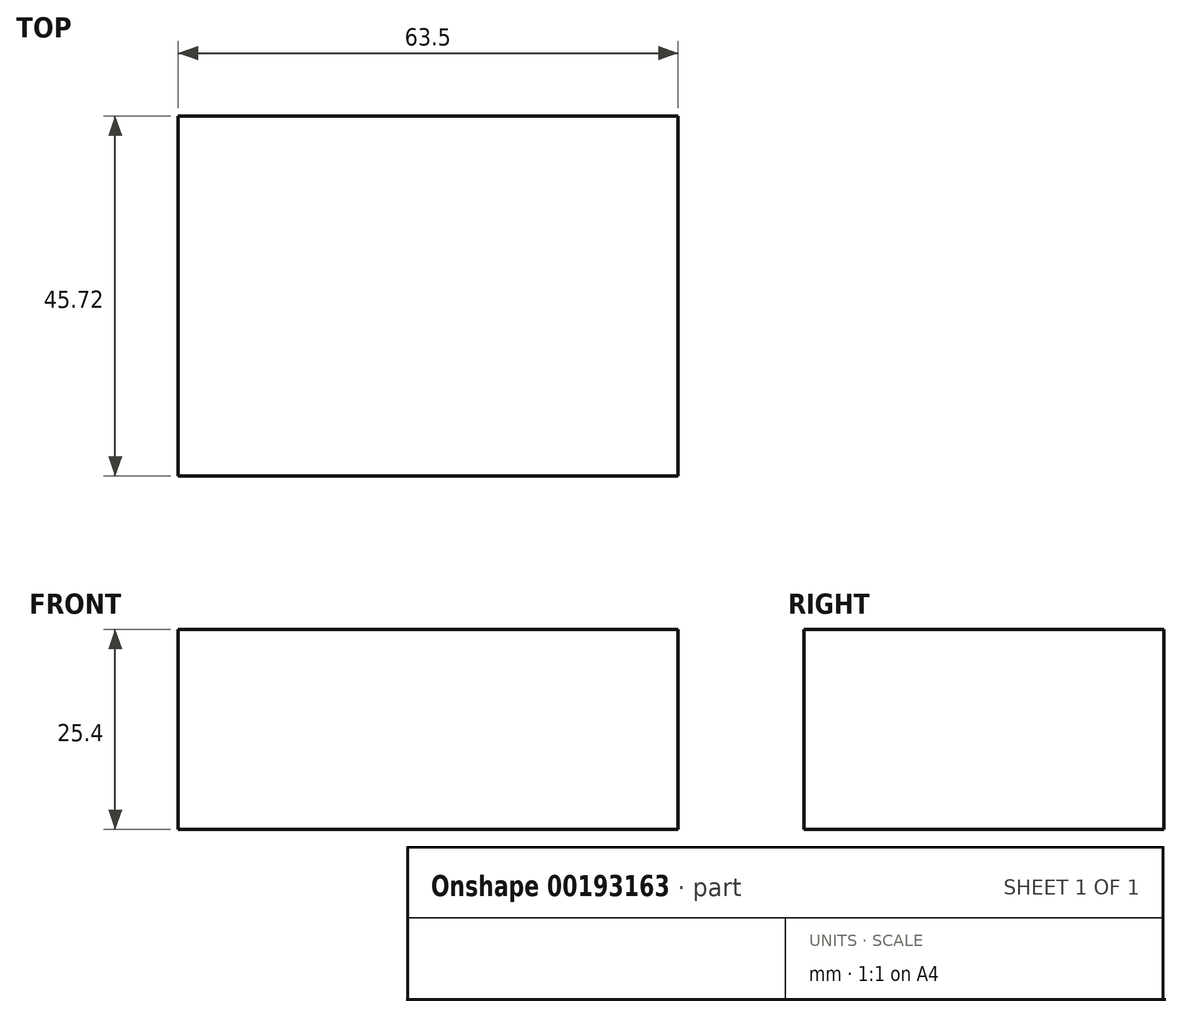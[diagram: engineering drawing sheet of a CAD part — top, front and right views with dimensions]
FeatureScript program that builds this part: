
annotation { "Feature Type Name" : "Feature", "Feature Type Description" : "" }
export const myFeature = defineFeature(function(context is Context, id is Id, definition is map)
    precondition{}
    {
        {
            var Q0;
            Q0=qCreatedBy(makeId("Top.planeOp"),FACE);
            var sketch = newSketch(context, id + "F0", { "sketchPlane" : qUnion([Q0])});
            skLineSegment(sketch, "E0.bottom", {"start": v(0, 0) * mm, "end": v(63.5, 0) * mm});
            skLineSegment(sketch, "E0.top", {"start": v(0, -45.72) * mm, "end": v(63.5, -45.72) * mm});
            skLineSegment(sketch, "E0.left", {"start": v(0, 0) * mm, "end": v(0, -45.72) * mm});
            skLineSegment(sketch, "E0.right", {"start": v(63.5, 0) * mm, "end": v(63.5, -45.72) * mm});
            skSolve(sketch);
        }
        {
            var Q0;
            Q0 = qSketchRegion(id + "F0", true);
            extrude(context, id + "F1", {"entities" : qUnion([Q0]), "endBound" : BoundingType.SYMMETRIC, "depth" : 25.4 * mm});
        }
    });
